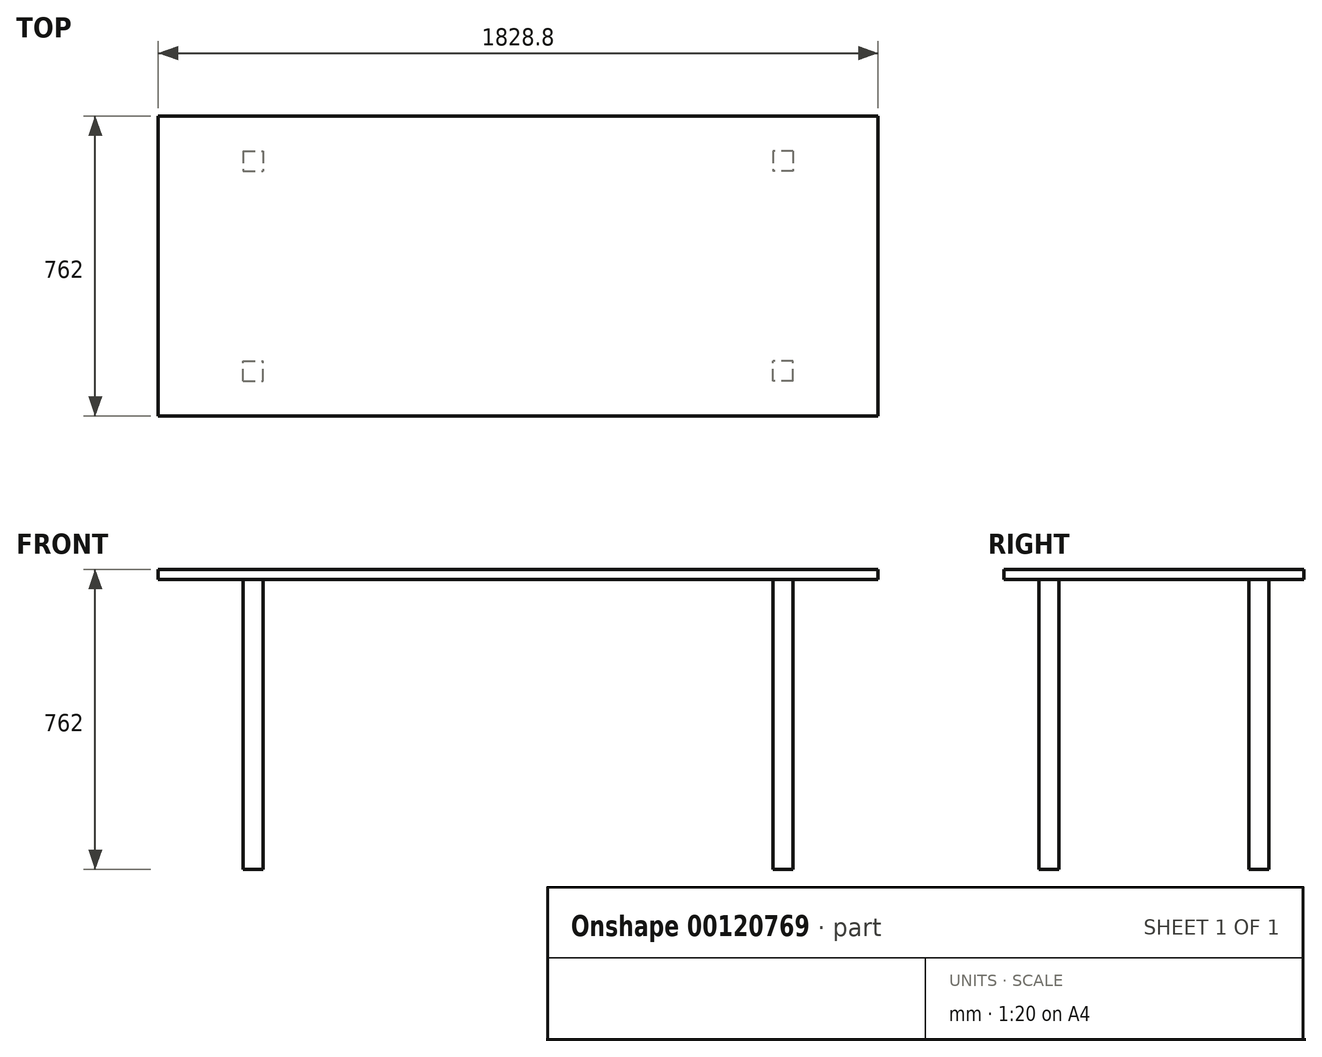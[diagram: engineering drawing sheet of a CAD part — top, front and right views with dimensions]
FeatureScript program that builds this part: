
annotation { "Feature Type Name" : "Feature", "Feature Type Description" : "" }
export const myFeature = defineFeature(function(context is Context, id is Id, definition is map)
    precondition{}
    {
        {
            var Q0;
            Q0=qCreatedBy(makeId("Top.planeOp"),FACE);
            var sketch = newSketch(context, id + "F0", { "sketchPlane" : qUnion([Q0])});
            skLineSegment(sketch, "E0.bottom", {"start": v(-914.4, 381) * mm, "end": v(914.4, 381) * mm});
            skLineSegment(sketch, "E0.top", {"start": v(-914.4, -381) * mm, "end": v(914.4, -381) * mm});
            skLineSegment(sketch, "E0.left", {"start": v(-914.4, 381) * mm, "end": v(-914.4, -381) * mm});
            skLineSegment(sketch, "E0.right", {"start": v(914.4, 381) * mm, "end": v(914.4, -381) * mm});
            skLineSegment(sketch, "E1", {"start": v(-914.4, 381) * mm, "end": v(914.4, -381) * mm, "construction": true});
            skSolve(sketch);
        }
        {
            var Q0;
            Q0 = qSketchRegion(id + "F0", true);
            extrude(context, id + "F1", {"entities" : qUnion([Q0]), "oppositeDirection" : true, "depth" : 25.4 * mm});
        }
        {
            var Q0;
            Q0=qCreatedBy(makeId("Top.planeOp"),FACE);
            var sketch = newSketch(context, id + "F2", { "sketchPlane" : qUnion([Q0])});
            skLineSegment(sketch, "E2.bottom", {"start": v(-698.5, 292.1) * mm, "end": v(698.5, 292.1) * mm, "construction": true});
            skLineSegment(sketch, "E2.top", {"start": v(-698.5, -292.1) * mm, "end": v(698.5, -292.1) * mm, "construction": true});
            skLineSegment(sketch, "E2.left", {"start": v(-698.5, 292.1) * mm, "end": v(-698.5, -292.1) * mm, "construction": true});
            skLineSegment(sketch, "E2.right", {"start": v(698.5, 292.1) * mm, "end": v(698.5, -292.1) * mm, "construction": true});
            skLineSegment(sketch, "E3.bottom", {"start": v(698.5, 292.1) * mm, "end": v(647.7, 292.1) * mm});
            skLineSegment(sketch, "E3.top", {"start": v(698.5, 241.3) * mm, "end": v(647.7, 241.3) * mm});
            skLineSegment(sketch, "E3.left", {"start": v(698.5, 292.1) * mm, "end": v(698.5, 241.3) * mm});
            skLineSegment(sketch, "E3.right", {"start": v(647.7, 292.1) * mm, "end": v(647.7, 241.3) * mm});
            skLineSegment(sketch, "E4.bottom", {"start": v(698.5, -292.1) * mm, "end": v(647.7, -292.1) * mm});
            skLineSegment(sketch, "E4.top", {"start": v(698.5, -241.3) * mm, "end": v(647.7, -241.3) * mm});
            skLineSegment(sketch, "E4.left", {"start": v(698.5, -292.1) * mm, "end": v(698.5, -241.3) * mm});
            skLineSegment(sketch, "E4.right", {"start": v(647.7, -292.1) * mm, "end": v(647.7, -241.3) * mm});
            skLineSegment(sketch, "E5.bottom", {"start": v(-698.5, -292.1) * mm, "end": v(-647.7, -292.1) * mm});
            skLineSegment(sketch, "E5.top", {"start": v(-698.5, -241.3) * mm, "end": v(-647.7, -241.3) * mm});
            skLineSegment(sketch, "E5.left", {"start": v(-698.5, -292.1) * mm, "end": v(-698.5, -241.3) * mm});
            skLineSegment(sketch, "E5.right", {"start": v(-647.7, -292.1) * mm, "end": v(-647.7, -241.3) * mm});
            skLineSegment(sketch, "E6.bottom", {"start": v(-698.5, 292.1) * mm, "end": v(-647.7, 292.1) * mm});
            skLineSegment(sketch, "E6.top", {"start": v(-698.5, 241.3) * mm, "end": v(-647.7, 241.3) * mm});
            skLineSegment(sketch, "E6.left", {"start": v(-698.5, 292.1) * mm, "end": v(-698.5, 241.3) * mm});
            skLineSegment(sketch, "E6.right", {"start": v(-647.7, 292.1) * mm, "end": v(-647.7, 241.3) * mm});
            skLineSegment(sketch, "E7", {"start": v(-698.5, 292.1) * mm, "end": v(698.5, -292.1) * mm, "construction": true});
            skSolve(sketch);
        }
        {
            var Q0;
            Q0 = qSketchRegion(id + "F2", true);
            extrude(context, id + "F3", {"entities" : qUnion([Q0]), "operationType" : NewBodyOperationType.ADD, "oppositeDirection" : true, "depth" : 762 * mm});
        }
    });
